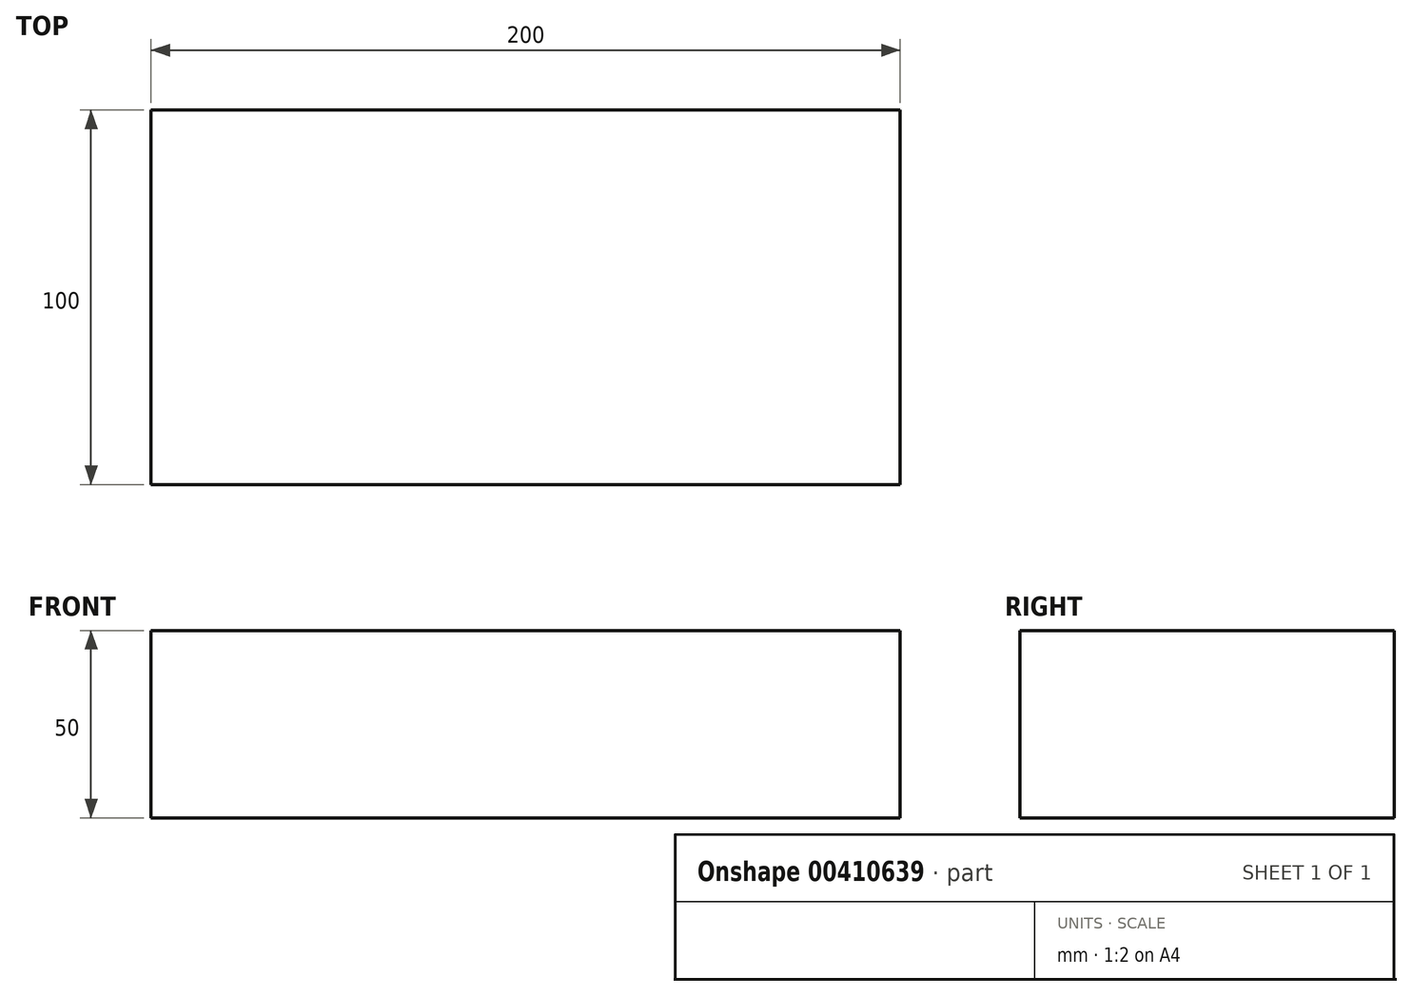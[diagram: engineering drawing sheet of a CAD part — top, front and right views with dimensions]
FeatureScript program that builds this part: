
annotation { "Feature Type Name" : "Feature", "Feature Type Description" : "" }
export const myFeature = defineFeature(function(context is Context, id is Id, definition is map)
    precondition{}
    {
        {
            var Q0;
            Q0=qCreatedBy(makeId("Front.planeOp"),FACE);
            var sketch = newSketch(context, id + "F0", { "sketchPlane" : qUnion([Q0])});
            skLineSegment(sketch, "E0.bottom", {"start": v(100, 25) * mm, "end": v(-100, 25) * mm});
            skLineSegment(sketch, "E0.top", {"start": v(100, -25) * mm, "end": v(-100, -25) * mm});
            skLineSegment(sketch, "E0.left", {"start": v(100, 25) * mm, "end": v(100, -25) * mm});
            skLineSegment(sketch, "E0.right", {"start": v(-100, 25) * mm, "end": v(-100, -25) * mm});
            skPoint(sketch, "E0.middle", {"position": v(0, 0) * mm});
            skSolve(sketch);
        }
        {
            var Q0;
            Q0 = qSketchRegion(id + "F0", true);
            extrude(context, id + "F1", {"entities" : qUnion([Q0]), "endBound" : BoundingType.SYMMETRIC, "depth" : 100 * mm});
        }
    });
